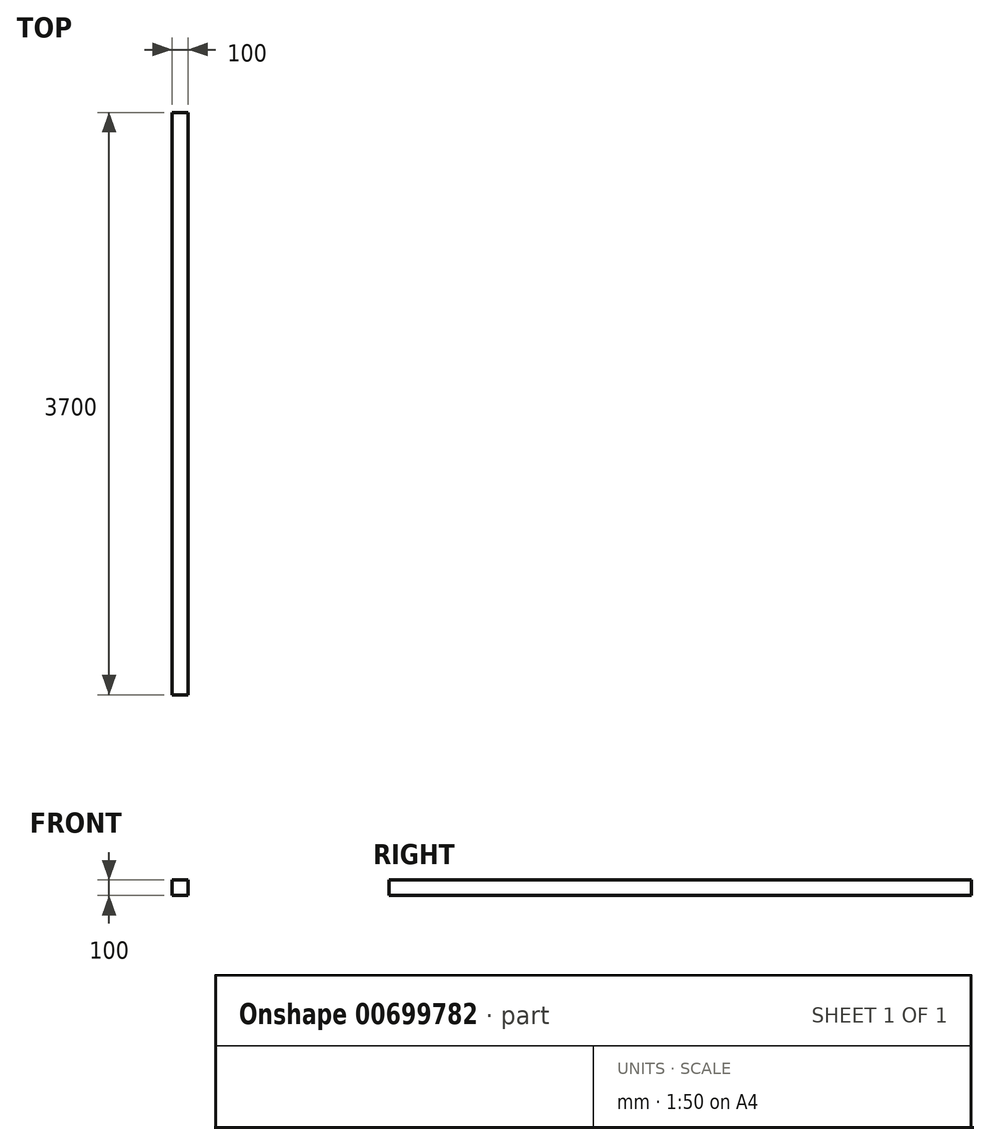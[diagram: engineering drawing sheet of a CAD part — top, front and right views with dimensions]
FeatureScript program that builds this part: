
annotation { "Feature Type Name" : "Feature", "Feature Type Description" : "" }
export const myFeature = defineFeature(function(context is Context, id is Id, definition is map)
    precondition{}
    {
        {
            var Q0;
            Q0=qCreatedBy(makeId("Front.planeOp"),FACE);
            var sketch = newSketch(context, id + "F0", { "sketchPlane" : qUnion([Q0])});
            skLineSegment(sketch, "E0.bottom", {"start": v(-50, 50) * mm, "end": v(50, 50) * mm});
            skLineSegment(sketch, "E0.top", {"start": v(-50, -50) * mm, "end": v(50, -50) * mm});
            skLineSegment(sketch, "E0.left", {"start": v(-50, 50) * mm, "end": v(-50, -50) * mm});
            skLineSegment(sketch, "E0.right", {"start": v(50, 50) * mm, "end": v(50, -50) * mm});
            skPoint(sketch, "E0.middle", {"position": v(0, 0) * mm});
            skSolve(sketch);
        }
        {
            var Q0;
            Q0=makeQuery(id+"F0.imprint","IMPRINT",FACE,{"disambiguationData":[TD([[makeQuery(id+"F0.imprint","IMPRINT",EDGE,{"derivedFrom":sQuery(id+"F0.wireOp",EDGE,"E0.bottom")}),-1.0]])]});
            extrude(context, id + "F1", {"entities" : qUnion([Q0]), "oppositeDirection" : true, "depth" : 3700 * mm, "offsetDistance" : 25 * mm});
        }
    });
